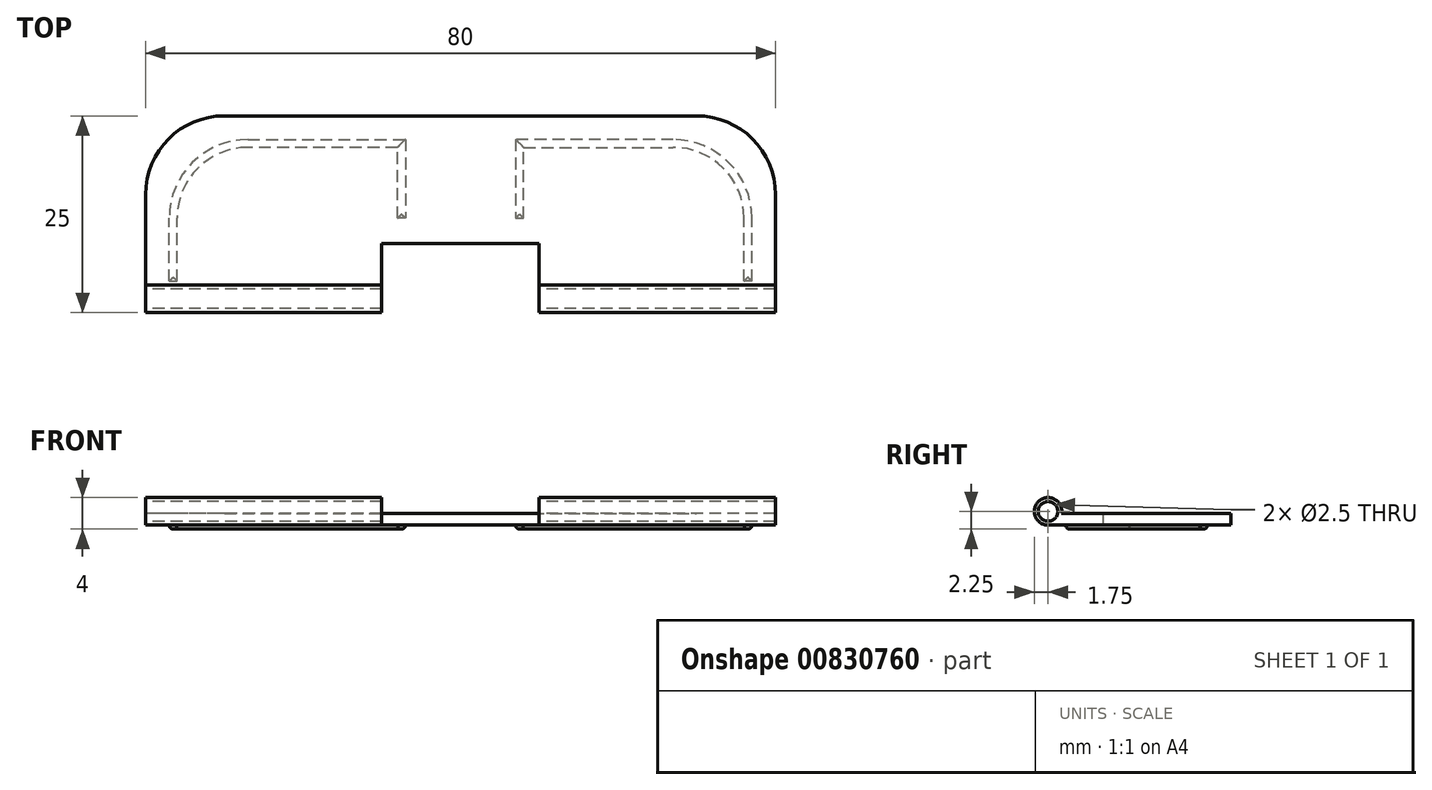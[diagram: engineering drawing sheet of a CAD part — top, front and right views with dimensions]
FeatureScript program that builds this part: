
annotation { "Feature Type Name" : "Feature", "Feature Type Description" : "" }
export const myFeature = defineFeature(function(context is Context, id is Id, definition is map)
    precondition{}
    {
        {
            var Q0;
            Q0=qCreatedBy(makeId("Top.planeOp"),FACE);
            var sketch = newSketch(context, id + "F0", { "sketchPlane" : qUnion([Q0])});
            skLineSegment(sketch, "E0.bottom", {"start": v(-40, 12.5) * mm, "end": v(40, 12.5) * mm});
            skLineSegment(sketch, "E0.top", {"start": v(-40, -12.5) * mm, "end": v(40, -12.5) * mm});
            skLineSegment(sketch, "E0.left", {"start": v(-40, 12.5) * mm, "end": v(-40, -12.5) * mm});
            skLineSegment(sketch, "E0.right", {"start": v(40, 12.5) * mm, "end": v(40, -12.5) * mm});
            skSolve(sketch);
        }
        {
            var Q0;
            Q0=makeQuery(id+"F0.imprint","IMPRINT",FACE,{"disambiguationData":[TD([[makeQuery(id+"F0.imprint","IMPRINT",EDGE,{"derivedFrom":sQuery(id+"F0.wireOp",EDGE,"E0.bottom")}),-1.0]])]});
            extrude(context, id + "F1", {"entities" : qUnion([Q0]), "depth" : 1.5 * mm, "offsetDistance" : 25 * mm});
        }
        {
            var Q0;
            Q0=makeQuery(id+"F1.opExtrude","SWEPT_EDGE",EDGE,{"disambiguationData":[OSD([sQuery(id+"F0.wireOp",EDGE,"E0.bottom"),sQuery(id+"F0.wireOp",EDGE,"E0.left")])]});
            var Q1;
            Q1=makeQuery(id+"F1.opExtrude","SWEPT_EDGE",EDGE,{"disambiguationData":[OSD([sQuery(id+"F0.wireOp",EDGE,"E0.bottom"),sQuery(id+"F0.wireOp",EDGE,"E0.right")])]});
            fillet(context, id + "F2", {"entities" : qUnion([Q0, Q1]), "radius" : 10 * mm, "tangentPropagation" : true, "allowEdgeOverflow" : false});
        }
        {
            var Q0;
            Q0=makeQuery(id+"F1.opExtrude","SWEPT_FACE",FACE,{"disambiguationData":[OSD([sQuery(id+"F0.wireOp",EDGE,"E0.left")])]});
            var sketch = newSketch(context, id + "F3", { "sketchPlane" : qUnion([Q0])});
            skCircle(sketch, "E1", {"center": v(10.75, 1.75) * mm, "radius": 1.75 * mm});
            skCircle(sketch, "E2", {"center": v(10.75, 1.75) * mm, "radius": 1.25 * mm});
            skSolve(sketch);
        }
        {
            var Q0;
            {var subQ0=sQuery(id+"F3.wireOp",EDGE,"E1");var subQ1=sQuery(id+"F0.wireOp",EDGE,"E0.left");var subQ4=makeQuery(id+"F1.opExtrude","CAP_EDGE",EDGE,{"disambiguationData":[OSD([subQ1])],"isStart":true});var subQ5=makeQuery(id+"F3.imprint","INTERSECT",VERTEX,{"derivedFrom":[subQ4,subQ0]});Q0=makeQuery(id+"F3.imprint","IMPRINT",FACE,{"disambiguationData":[TD([[makeQuery(id+"F3.imprint","IMPRINT",EDGE,{"disambiguationData":[TD([[subQ5,-1.0]])],"derivedFrom":subQ0}),-1.0]])]});}
            var Q1;
            {var subQ0=sQuery(id+"F3.wireOp",EDGE,"E1");var subQ1=sQuery(id+"F0.wireOp",EDGE,"E0.left");var subQ2=makeQuery(id+"F1.opExtrude","CAP_EDGE",EDGE,{"disambiguationData":[OSD([subQ1])],"isStart":false});var subQ3=makeQuery(id+"F3.imprint","INTERSECT",VERTEX,{"disambiguationData":[OD(0.0)],"derivedFrom":[subQ2,subQ0]});Q1=makeQuery(id+"F3.imprint","IMPRINT",FACE,{"disambiguationData":[TD([[makeQuery(id+"F3.imprint","IMPRINT",EDGE,{"disambiguationData":[TD([[subQ3,1.0]])],"derivedFrom":subQ0}),-1.0]])]});}
            extrude(context, id + "F4", {"entities" : qUnion([Q0, Q1]), "operationType" : NewBodyOperationType.REMOVE, "oppositeDirection" : true, "depth" : 80 * mm, "offsetDistance" : 25 * mm});
        }
        {
            var Q0;
            Q0 = qSketchRegion(id + "F3", true);
            extrude(context, id + "F5", {"entities" : qUnion([Q0]), "operationType" : NewBodyOperationType.ADD, "oppositeDirection" : true, "depth" : 80 * mm, "offsetDistance" : 25 * mm});
        }
        {
            var Q0;
            {var subQ0=sQuery(id+"F3.wireOp",EDGE,"E2");var subQ1=makeQuery(id+"F1.opExtrude","CAP_EDGE",EDGE,{"disambiguationData":[OSD([sQuery(id+"F0.wireOp",EDGE,"E0.left")])],"isStart":false});var subQ2=makeQuery(id+"F3.imprint","INTERSECT",VERTEX,{"disambiguationData":[OD(0.0)],"derivedFrom":[subQ1,subQ0]});Q0=makeQuery(id+"F3.imprint","IMPRINT",FACE,{"disambiguationData":[TD([[makeQuery(id+"F3.imprint","IMPRINT",EDGE,{"disambiguationData":[TD([[subQ2,-1.0]])],"derivedFrom":subQ0}),1.0]])]});}
            var Q1;
            {var subQ0=sQuery(id+"F3.wireOp",EDGE,"E2");var subQ1=makeQuery(id+"F1.opExtrude","CAP_EDGE",EDGE,{"disambiguationData":[OSD([sQuery(id+"F0.wireOp",EDGE,"E0.left")])],"isStart":false});var subQ2=makeQuery(id+"F3.imprint","INTERSECT",VERTEX,{"disambiguationData":[OD(0.0)],"derivedFrom":[subQ1,subQ0]});Q1=makeQuery(id+"F3.imprint","IMPRINT",FACE,{"disambiguationData":[TD([[makeQuery(id+"F3.imprint","IMPRINT",EDGE,{"disambiguationData":[TD([[subQ2,1.0]])],"derivedFrom":subQ0}),1.0]])]});}
            extrude(context, id + "F6", {"entities" : qUnion([Q0, Q1]), "operationType" : NewBodyOperationType.REMOVE, "oppositeDirection" : true, "depth" : 80 * mm, "offsetDistance" : 25 * mm});
        }
        {
            var Q0;
            Q0=makeQuery(id+"F1.opExtrude","CAP_FACE",FACE,{"disambiguationData":[OSD([sQuery(id+"F0.wireOp",EDGE,"E0.bottom"),sQuery(id+"F0.wireOp",EDGE,"E0.top"),sQuery(id+"F0.wireOp",EDGE,"E0.left"),sQuery(id+"F0.wireOp",EDGE,"E0.right")])],"isStart":true});
            var sketch = newSketch(context, id + "F7", { "sketchPlane" : qUnion([Q0])});
            skLineSegment(sketch, "E3.bottom", {"start": v(10, 29.43) * mm, "end": v(-10, 29.43) * mm});
            skLineSegment(sketch, "E3.top", {"start": v(10, 3.75) * mm, "end": v(-10, 3.75) * mm});
            skLineSegment(sketch, "E3.left", {"start": v(10, 29.43) * mm, "end": v(10, 3.75) * mm});
            skLineSegment(sketch, "E3.right", {"start": v(-10, 29.43) * mm, "end": v(-10, 3.75) * mm});
            skSolve(sketch);
        }
        {
            var Q0;
            {var subQ0=sQuery(id+"F7.wireOp",EDGE,"E3.bottom");Q0=makeQuery(id+"F7.imprint","IMPRINT",FACE,{"disambiguationData":[TD([[makeQuery(id+"F7.imprint","IMPRINT",EDGE,{"derivedFrom":subQ0}),1.0]])]});}
            var Q1;
            {var subQ0=sQuery(id+"F7.wireOp",EDGE,"E3.top");Q1=makeQuery(id+"F7.imprint","IMPRINT",FACE,{"disambiguationData":[TD([[makeQuery(id+"F7.imprint","IMPRINT",EDGE,{"derivedFrom":subQ0}),-1.0]])]});}
            extrude(context, id + "F8", {"entities" : qUnion([Q0, Q1]), "operationType" : NewBodyOperationType.REMOVE, "oppositeDirection" : true, "depth" : 25 * mm, "offsetDistance" : 25 * mm});
        }
        {
            var Q0;
            Q0=makeQuery(id+"F1.opExtrude","CAP_FACE",FACE,{"disambiguationData":[OSD([sQuery(id+"F0.wireOp",EDGE,"E0.bottom"),sQuery(id+"F0.wireOp",EDGE,"E0.top"),sQuery(id+"F0.wireOp",EDGE,"E0.left"),sQuery(id+"F0.wireOp",EDGE,"E0.right")])],"isStart":true});
            var sketch = newSketch(context, id + "F9", { "sketchPlane" : qUnion([Q0])});
            skLineSegment(sketch, "E4", {"start": v(-37, 8.5) * mm, "end": v(-37, 0.5) * mm});
            skLineSegment(sketch, "E5", {"start": v(-27, -9.5) * mm, "end": v(-7, -9.5) * mm});
            skLineSegment(sketch, "E6", {"start": v(-7, -9.5) * mm, "end": v(-7, 0.5) * mm});
            skPoint(sketch, "E7.visualSharp", {"position": v(-37, -9.5) * mm});
            skArc(sketch, "E7.filletArc", {"start": v(-37, 0.5) * mm, "mid": v(-34.07, -6.57) * mm, "end": v(-27, -9.5) * mm});
            skLineSegment(sketch, "E8", {"start": v(-37, 8.5) * mm, "end": v(-36, 8.5) * mm});
            skLineSegment(sketch, "E9", {"start": v(-36, 8.5) * mm, "end": v(-36, 0.5) * mm});
            skLineSegment(sketch, "E10", {"start": v(-7, 0.5) * mm, "end": v(-8, 0.5) * mm});
            skLineSegment(sketch, "E11", {"start": v(-8, 0.5) * mm, "end": v(-8, -8.5) * mm});
            skLineSegment(sketch, "E12", {"start": v(-8, -8.5) * mm, "end": v(-27, -8.5) * mm});
            skLineSegment(sketch, "E13", {"start": v(-36, 0.5) * mm, "end": v(-36, 0.5) * mm});
            skLineSegment(sketch, "E14", {"start": v(-27, -8.5) * mm, "end": v(-27, -8.5) * mm});
            skArc(sketch, "E15.filletArc", {"start": v(-36, 0.5) * mm, "mid": v(-33.36, -5.86) * mm, "end": v(-27, -8.5) * mm});
            skLineSegment(sketch, "E16.MirrorCS", {"start": v(7, 0.5) * mm, "end": v(8, 0.5) * mm});
            skLineSegment(sketch, "E17.MirrorCS", {"start": v(37, 8.5) * mm, "end": v(36, 8.5) * mm});
            skLineSegment(sketch, "E18.MirrorCS", {"start": v(36, 8.5) * mm, "end": v(36, 0.5) * mm});
            skArc(sketch, "E19.MirrorCS", {"start": v(37, 0.5) * mm, "mid": v(34.07, -6.57) * mm, "end": v(27, -9.5) * mm});
            skLineSegment(sketch, "E20.MirrorCS", {"start": v(7, -9.5) * mm, "end": v(7, 0.5) * mm});
            skLineSegment(sketch, "E21.MirrorCS", {"start": v(8, -8.5) * mm, "end": v(27, -8.5) * mm});
            skLineSegment(sketch, "E22.MirrorCS", {"start": v(27, -9.5) * mm, "end": v(7, -9.5) * mm});
            skLineSegment(sketch, "E23.MirrorCS", {"start": v(8, 0.5) * mm, "end": v(8, -8.5) * mm});
            skLineSegment(sketch, "E24.MirrorCS", {"start": v(37, 8.5) * mm, "end": v(37, 0.5) * mm});
            skPoint(sketch, "E25.MirrorP", {"position": v(37, -9.5) * mm});
            skArc(sketch, "E26.MirrorCS", {"start": v(36, 0.5) * mm, "mid": v(33.36, -5.86) * mm, "end": v(27, -8.5) * mm});
            skSolve(sketch);
        }
        {
            var Q0;
            Q0=makeQuery(id+"F9.imprint","IMPRINT",FACE,{"disambiguationData":[TD([[makeQuery(id+"F9.imprint","IMPRINT",EDGE,{"derivedFrom":sQuery(id+"F9.wireOp",EDGE,"E4")}),1.0]])]});
            var Q1;
            Q1=makeQuery(id+"F9.imprint","IMPRINT",FACE,{"disambiguationData":[TD([[makeQuery(id+"F9.imprint","IMPRINT",EDGE,{"derivedFrom":sQuery(id+"F9.wireOp",EDGE,"E16.MirrorCS")}),-1.0]])]});
            extrude(context, id + "F10", {"entities" : qUnion([Q0, Q1]), "operationType" : NewBodyOperationType.ADD, "depth" : 0.5 * mm, "offsetDistance" : 25 * mm});
        }
        {
            var Q0;
            Q0=makeQuery(id+"F10.opExtrude","CAP_FACE",FACE,{"disambiguationData":[OSD([sQuery(id+"F9.wireOp",EDGE,"E4"),sQuery(id+"F9.wireOp",EDGE,"E5"),sQuery(id+"F9.wireOp",EDGE,"E6"),sQuery(id+"F9.wireOp",EDGE,"E7.filletArc"),sQuery(id+"F9.wireOp",EDGE,"E8"),sQuery(id+"F9.wireOp",EDGE,"E9"),sQuery(id+"F9.wireOp",EDGE,"E10"),sQuery(id+"F9.wireOp",EDGE,"E11"),sQuery(id+"F9.wireOp",EDGE,"E12"),sQuery(id+"F9.wireOp",EDGE,"E15.filletArc")])],"isStart":false});
            var Q1;
            Q1=makeQuery(id+"F10.opExtrude","CAP_FACE",FACE,{"disambiguationData":[OSD([sQuery(id+"F9.wireOp",EDGE,"E16.MirrorCS"),sQuery(id+"F9.wireOp",EDGE,"E17.MirrorCS"),sQuery(id+"F9.wireOp",EDGE,"E18.MirrorCS"),sQuery(id+"F9.wireOp",EDGE,"E19.MirrorCS"),sQuery(id+"F9.wireOp",EDGE,"E20.MirrorCS"),sQuery(id+"F9.wireOp",EDGE,"E21.MirrorCS"),sQuery(id+"F9.wireOp",EDGE,"E22.MirrorCS"),sQuery(id+"F9.wireOp",EDGE,"E23.MirrorCS"),sQuery(id+"F9.wireOp",EDGE,"E24.MirrorCS"),sQuery(id+"F9.wireOp",EDGE,"E26.MirrorCS")])],"isStart":false});
            fillet(context, id + "F11", {"entities" : qUnion([Q0, Q1]), "radius" : 0.5 * mm, "tangentPropagation" : true, "allowEdgeOverflow" : false});
        }
    });
